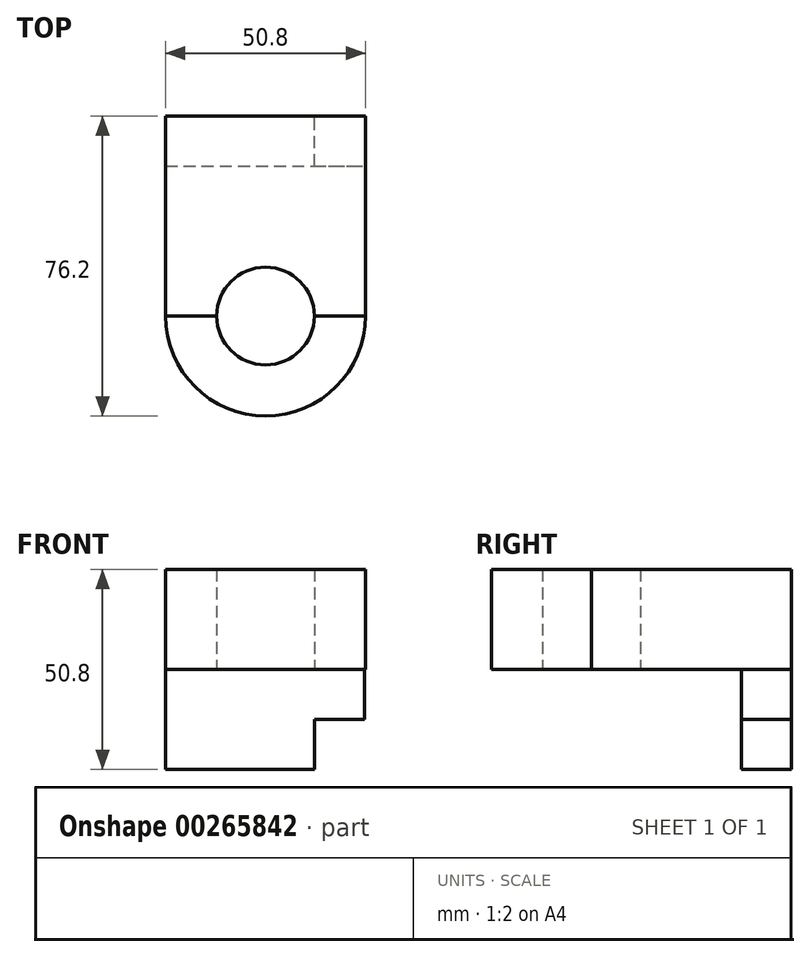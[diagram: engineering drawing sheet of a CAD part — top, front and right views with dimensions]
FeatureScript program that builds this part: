
annotation { "Feature Type Name" : "Feature", "Feature Type Description" : "" }
export const myFeature = defineFeature(function(context is Context, id is Id, definition is map)
    precondition{}
    {
        {
            var Q0;
            Q0=qCreatedBy(makeId("Top.planeOp"),FACE);
            var sketch = newSketch(context, id + "F0", { "sketchPlane" : qUnion([Q0])});
            skLineSegment(sketch, "E0.bottom", {"start": v(0, 0) * mm, "end": v(50.8, 0) * mm});
            skLineSegment(sketch, "E0.top", {"start": v(0, -50.8) * mm, "end": v(50.8, -50.8) * mm});
            skLineSegment(sketch, "E0.left", {"start": v(0, 0) * mm, "end": v(0, -50.8) * mm});
            skLineSegment(sketch, "E0.right", {"start": v(50.8, 0) * mm, "end": v(50.8, -50.8) * mm});
            skSolve(sketch);
        }
        {
            var Q0;
            Q0 = qSketchRegion(id + "F0", true);
            var Q1;
            Q1=makeQuery(id+"F0.imprint","IMPRINT",FACE,{"disambiguationData":[TD([[makeQuery(id+"F0.imprint","IMPRINT",EDGE,{"derivedFrom":sQuery(id+"F0.wireOp",EDGE,"E0.bottom")}),-1.0]])]});
            extrude(context, id + "F1", {"entities" : qUnion([Q0, Q1]), "depth" : 25.4 * mm});
        }
        {
            var Q0;
            Q0=qCreatedBy(makeId("Top.planeOp"),FACE);
            var sketch = newSketch(context, id + "F2", { "sketchPlane" : qUnion([Q0])});
            skLineSegment(sketch, "E1.bottom", {"start": v(0, 0) * mm, "end": v(50.51, 0) * mm});
            skLineSegment(sketch, "E1.top", {"start": v(0, -12.7) * mm, "end": v(50.51, -12.7) * mm});
            skLineSegment(sketch, "E1.left", {"start": v(0, 0) * mm, "end": v(0, -12.7) * mm});
            skLineSegment(sketch, "E1.right", {"start": v(50.51, 0) * mm, "end": v(50.51, -12.7) * mm});
            skSolve(sketch);
        }
        {
            var Q0;
            Q0=makeQuery(id+"F2.imprint","IMPRINT",FACE,{"disambiguationData":[TD([[makeQuery(id+"F2.imprint","IMPRINT",EDGE,{"derivedFrom":sQuery(id+"F2.wireOp",EDGE,"E1.bottom")}),-1.0]])]});
            extrude(context, id + "F3", {"entities" : qUnion([Q0]), "operationType" : NewBodyOperationType.ADD, "oppositeDirection" : true, "depth" : 25.4 * mm});
        }
        {
            var Q0;
            Q0=makeQuery(id+"F3.opExtrude","CAP_FACE",FACE,{"disambiguationData":[OSD([sQuery(id+"F2.wireOp",EDGE,"E1.bottom"),sQuery(id+"F2.wireOp",EDGE,"E1.top"),sQuery(id+"F2.wireOp",EDGE,"E1.left"),sQuery(id+"F2.wireOp",EDGE,"E1.right")])],"isStart":false});
            var sketch = newSketch(context, id + "F4", { "sketchPlane" : qUnion([Q0])});
            skLineSegment(sketch, "E2.bottom", {"start": v(50.51, 12.7) * mm, "end": v(37.81, 12.7) * mm});
            skLineSegment(sketch, "E2.top", {"start": v(50.51, 0) * mm, "end": v(37.81, 0) * mm});
            skLineSegment(sketch, "E2.left", {"start": v(50.51, 12.7) * mm, "end": v(50.51, 0) * mm});
            skLineSegment(sketch, "E2.right", {"start": v(37.81, 12.7) * mm, "end": v(37.81, 0) * mm});
            skSolve(sketch);
        }
        {
            var Q0;
            Q0=makeQuery(id+"F4.imprint","IMPRINT",FACE,{"disambiguationData":[TD([[makeQuery(id+"F4.imprint","IMPRINT",EDGE,{"derivedFrom":sQuery(id+"F4.wireOp",EDGE,"E2.bottom")}),-1.0]])]});
            extrude(context, id + "F5", {"entities" : qUnion([Q0]), "operationType" : NewBodyOperationType.REMOVE, "oppositeDirection" : true, "depth" : 12.7 * mm});
        }
        {
            var Q0;
            Q0=makeQuery(id+"F5.boolean.opBoolean","MERGE",FACE,{"derivedFrom":[makeQuery(id+"F1.opExtrude","CAP_FACE",FACE,{"disambiguationData":[OSD([sQuery(id+"F0.wireOp",EDGE,"E0.bottom"),sQuery(id+"F0.wireOp",EDGE,"E0.top"),sQuery(id+"F0.wireOp",EDGE,"E0.left"),sQuery(id+"F0.wireOp",EDGE,"E0.right")])],"isStart":true}),makeQuery(id+"F5.opExtrude","CAP_FACE",FACE,{"disambiguationData":[OSD([sQuery(id+"F4.wireOp",EDGE,"E2.bottom"),sQuery(id+"F4.wireOp",EDGE,"E2.top"),sQuery(id+"F4.wireOp",EDGE,"E2.left"),sQuery(id+"F4.wireOp",EDGE,"E2.right")])],"isStart":false})]});
            var sketch = newSketch(context, id + "F6", { "sketchPlane" : qUnion([Q0])});
            skCircle(sketch, "E3", {"center": v(25.4, 50.8) * mm, "radius": 25.4 * mm});
            skSolve(sketch);
        }
        {
            var Q0;
            {var subQ1=makeQuery(id+"F1.opExtrude","CAP_EDGE",EDGE,{"disambiguationData":[OSD([sQuery(id+"F0.wireOp",EDGE,"E0.top")])],"isStart":true});Q0=makeQuery(id+"F6.imprint","IMPRINT",FACE,{"disambiguationData":[TD([[makeQuery(id+"F6.imprint","IMPRINT",EDGE,{"derivedFrom":subQ1}),1.0]])]});}
            extrude(context, id + "F7", {"entities" : qUnion([Q0]), "oppositeDirection" : true, "depth" : 25.4 * mm});
        }
        {
            var Q0;
            Q0=makeQuery(id+"F5.boolean.opBoolean","MERGE",FACE,{"derivedFrom":[makeQuery(id+"F1.opExtrude","CAP_FACE",FACE,{"disambiguationData":[OSD([sQuery(id+"F0.wireOp",EDGE,"E0.bottom"),sQuery(id+"F0.wireOp",EDGE,"E0.top"),sQuery(id+"F0.wireOp",EDGE,"E0.left"),sQuery(id+"F0.wireOp",EDGE,"E0.right")])],"isStart":true}),makeQuery(id+"F5.opExtrude","CAP_FACE",FACE,{"disambiguationData":[OSD([sQuery(id+"F4.wireOp",EDGE,"E2.bottom"),sQuery(id+"F4.wireOp",EDGE,"E2.top"),sQuery(id+"F4.wireOp",EDGE,"E2.left"),sQuery(id+"F4.wireOp",EDGE,"E2.right")])],"isStart":false})]});
            var sketch = newSketch(context, id + "F8", { "sketchPlane" : qUnion([Q0])});
            skCircle(sketch, "E4", {"center": v(25.4, 50.8) * mm, "radius": 12.41 * mm});
            skSolve(sketch);
        }
        {
            var Q0;
            {var subQ0=sQuery(id+"F8.wireOp",EDGE,"E4");var subQ1=makeQuery(id+"F1.opExtrude","CAP_EDGE",EDGE,{"disambiguationData":[OSD([sQuery(id+"F0.wireOp",EDGE,"E0.top")])],"isStart":true});var subQ2=makeQuery(id+"F8.imprint","INTERSECT",VERTEX,{"disambiguationData":[OD(0.0)],"derivedFrom":[subQ1,subQ0]});Q0=makeQuery(id+"F8.imprint","IMPRINT",FACE,{"disambiguationData":[TD([[makeQuery(id+"F8.imprint","IMPRINT",EDGE,{"disambiguationData":[TD([[subQ2,-1.0]])],"derivedFrom":subQ0}),1.0]])]});}
            var Q1;
            {var subQ0=sQuery(id+"F8.wireOp",EDGE,"E4");var subQ1=makeQuery(id+"F1.opExtrude","CAP_EDGE",EDGE,{"disambiguationData":[OSD([sQuery(id+"F0.wireOp",EDGE,"E0.top")])],"isStart":true});var subQ2=makeQuery(id+"F8.imprint","INTERSECT",VERTEX,{"disambiguationData":[OD(0.0)],"derivedFrom":[subQ1,subQ0]});Q1=makeQuery(id+"F8.imprint","IMPRINT",FACE,{"disambiguationData":[TD([[makeQuery(id+"F8.imprint","IMPRINT",EDGE,{"disambiguationData":[TD([[subQ2,1.0]])],"derivedFrom":subQ0}),1.0]])]});}
            extrude(context, id + "F9", {"entities" : qUnion([Q0, Q1]), "operationType" : NewBodyOperationType.REMOVE, "oppositeDirection" : true, "depth" : 25.4 * mm});
        }
        {
            var Q0;
            Q0 = qSketchRegion(id + "F8", true);
            extrude(context, id + "F10", {"entities" : qUnion([Q0]), "operationType" : NewBodyOperationType.REMOVE, "oppositeDirection" : true, "depth" : 25.4 * mm});
        }
        {
            var Q0;
            Q0 = qSketchRegion(id + "F8", true);
            extrude(context, id + "F11", {"entities" : qUnion([Q0]), "operationType" : NewBodyOperationType.REMOVE, "oppositeDirection" : true, "depth" : 25.4 * mm});
        }
    });
